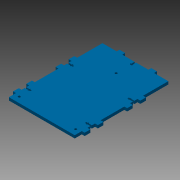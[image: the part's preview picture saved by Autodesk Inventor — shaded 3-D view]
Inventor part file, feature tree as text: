
AUTODESK INVENTOR PART (.ipt)
format: ipt  version: 2013 (Build 170138000, 138)  size: 188,928 bytes
history: native  units: mm
features: extrude x1, sketch x1
ambient origin geometry x8: Origin, YZ Plane, XZ Plane, XY Plane, X Axis, Y Axis, Z Axis, Center Point
bodies: Solid1 (feature_tree)
feature tree (2):
  extrude  "Extrusion1"  [1 undecoded]
  sketch  "Sketch1"  dims[d0=6.0mm d1=0.0mm]
note: 1 required parameter value undecoded (feature->parameter linkage not recoverable at this tier; creation-order binding heuristic only, values carry confidence <= 0.55)
